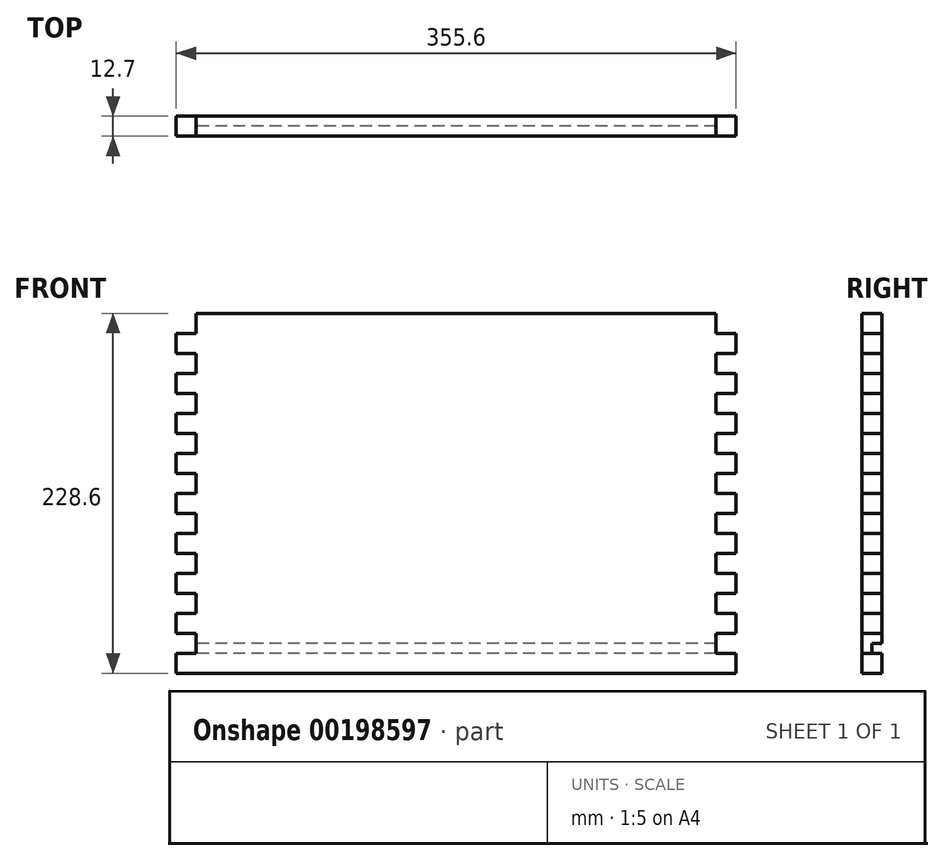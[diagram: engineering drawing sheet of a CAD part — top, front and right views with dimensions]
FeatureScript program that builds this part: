
annotation { "Feature Type Name" : "Feature", "Feature Type Description" : "" }
export const myFeature = defineFeature(function(context is Context, id is Id, definition is map)
    precondition{}
    {
        {
            var Q0;
            Q0=qCreatedBy(makeId("Front.planeOp"),FACE);
            var sketch = newSketch(context, id + "F0", { "sketchPlane" : qUnion([Q0])});
            skLineSegment(sketch, "E0.bottom", {"start": v(0, 0) * mm, "end": v(355.6, 0) * mm});
            skLineSegment(sketch, "E0.top", {"start": v(0, 228.6) * mm, "end": v(355.6, 228.6) * mm});
            skLineSegment(sketch, "E0.left", {"start": v(0, 0) * mm, "end": v(0, 228.6) * mm});
            skLineSegment(sketch, "E0.right", {"start": v(355.6, 0) * mm, "end": v(355.6, 228.6) * mm});
            skSolve(sketch);
        }
        {
            var Q0;
            Q0 = qSketchRegion(id + "F0", true);
            extrude(context, id + "F1", {"entities" : qUnion([Q0]), "depth" : 12.7 * mm});
        }
        {
            var Q0;
            Q0=makeQuery(id+"F1.opExtrude","CAP_FACE",FACE,{"disambiguationData":[OSD([sQuery(id+"F0.wireOp",EDGE,"E0.bottom"),sQuery(id+"F0.wireOp",EDGE,"E0.top"),sQuery(id+"F0.wireOp",EDGE,"E0.left"),sQuery(id+"F0.wireOp",EDGE,"E0.right")])],"isStart":false});
            var sketch = newSketch(context, id + "F2", { "sketchPlane" : qUnion([Q0])});
            skLineSegment(sketch, "E1", {"start": v(0, 228.6) * mm, "end": v(12.7, 228.6) * mm});
            skLineSegment(sketch, "E2.bottom", {"start": v(12.7, 228.6) * mm, "end": v(0, 228.6) * mm});
            skLineSegment(sketch, "E2.top", {"start": v(12.7, 215.9) * mm, "end": v(0, 215.9) * mm});
            skLineSegment(sketch, "E2.left", {"start": v(12.7, 228.6) * mm, "end": v(12.7, 215.9) * mm});
            skLineSegment(sketch, "E2.right", {"start": v(0, 228.6) * mm, "end": v(0, 215.9) * mm});
            skLineSegment(sketch, "E3.0.1.0", {"start": v(12.7, 190.5) * mm, "end": v(0, 190.5) * mm});
            skLineSegment(sketch, "E3.0.1.1", {"start": v(12.7, 203.2) * mm, "end": v(12.7, 190.5) * mm});
            skLineSegment(sketch, "E3.0.1.2", {"start": v(12.7, 203.2) * mm, "end": v(0, 203.2) * mm});
            skLineSegment(sketch, "E3.0.1.3", {"start": v(0, 203.2) * mm, "end": v(0, 190.5) * mm});
            skLineSegment(sketch, "E3.0.2.0", {"start": v(12.7, 165.1) * mm, "end": v(0, 165.1) * mm});
            skLineSegment(sketch, "E3.0.2.1", {"start": v(12.7, 177.8) * mm, "end": v(12.7, 165.1) * mm});
            skLineSegment(sketch, "E3.0.2.2", {"start": v(12.7, 177.8) * mm, "end": v(0, 177.8) * mm});
            skLineSegment(sketch, "E3.0.2.3", {"start": v(0, 177.8) * mm, "end": v(0, 165.1) * mm});
            skLineSegment(sketch, "E3.0.3.0", {"start": v(12.7, 139.7) * mm, "end": v(0, 139.7) * mm});
            skLineSegment(sketch, "E3.0.3.1", {"start": v(12.7, 152.4) * mm, "end": v(12.7, 139.7) * mm});
            skLineSegment(sketch, "E3.0.3.2", {"start": v(12.7, 152.4) * mm, "end": v(0, 152.4) * mm});
            skLineSegment(sketch, "E3.0.3.3", {"start": v(0, 152.4) * mm, "end": v(0, 139.7) * mm});
            skLineSegment(sketch, "E3.0.4.0", {"start": v(12.7, 114.3) * mm, "end": v(0, 114.3) * mm});
            skLineSegment(sketch, "E3.0.4.1", {"start": v(12.7, 127) * mm, "end": v(12.7, 114.3) * mm});
            skLineSegment(sketch, "E3.0.4.2", {"start": v(12.7, 127) * mm, "end": v(0, 127) * mm});
            skLineSegment(sketch, "E3.0.4.3", {"start": v(0, 127) * mm, "end": v(0, 114.3) * mm});
            skLineSegment(sketch, "E3.0.5.0", {"start": v(12.7, 88.9) * mm, "end": v(0, 88.9) * mm});
            skLineSegment(sketch, "E3.0.5.1", {"start": v(12.7, 101.6) * mm, "end": v(12.7, 88.9) * mm});
            skLineSegment(sketch, "E3.0.5.2", {"start": v(12.7, 101.6) * mm, "end": v(0, 101.6) * mm});
            skLineSegment(sketch, "E3.0.5.3", {"start": v(0, 101.6) * mm, "end": v(0, 88.9) * mm});
            skLineSegment(sketch, "E3.0.6.0", {"start": v(12.7, 63.5) * mm, "end": v(0, 63.5) * mm});
            skLineSegment(sketch, "E3.0.6.1", {"start": v(12.7, 76.2) * mm, "end": v(12.7, 63.5) * mm});
            skLineSegment(sketch, "E3.0.6.2", {"start": v(12.7, 76.2) * mm, "end": v(0, 76.2) * mm});
            skLineSegment(sketch, "E3.0.6.3", {"start": v(0, 76.2) * mm, "end": v(0, 63.5) * mm});
            skLineSegment(sketch, "E3.0.7.0", {"start": v(12.7, 38.1) * mm, "end": v(0, 38.1) * mm});
            skLineSegment(sketch, "E3.0.7.1", {"start": v(12.7, 50.8) * mm, "end": v(12.7, 38.1) * mm});
            skLineSegment(sketch, "E3.0.7.2", {"start": v(12.7, 50.8) * mm, "end": v(0, 50.8) * mm});
            skLineSegment(sketch, "E3.0.7.3", {"start": v(0, 50.8) * mm, "end": v(0, 38.1) * mm});
            skLineSegment(sketch, "E3.0.8.0", {"start": v(12.7, 12.7) * mm, "end": v(0, 12.7) * mm});
            skLineSegment(sketch, "E3.0.8.1", {"start": v(12.7, 25.4) * mm, "end": v(12.7, 12.7) * mm});
            skLineSegment(sketch, "E3.0.8.2", {"start": v(12.7, 25.4) * mm, "end": v(0, 25.4) * mm});
            skLineSegment(sketch, "E3.0.8.3", {"start": v(0, 25.4) * mm, "end": v(0, 12.7) * mm});
            skLineSegment(sketch, "E3.1.1.0", {"start": v(12.7, 190.5) * mm, "end": v(0, 190.5) * mm});
            skLineSegment(sketch, "E3.1.1.1", {"start": v(12.7, 203.2) * mm, "end": v(12.7, 190.5) * mm});
            skLineSegment(sketch, "E3.1.1.2", {"start": v(12.7, 203.2) * mm, "end": v(0, 203.2) * mm});
            skLineSegment(sketch, "E3.1.1.3", {"start": v(0, 203.2) * mm, "end": v(0, 190.5) * mm});
            skLineSegment(sketch, "E3.1.2.0", {"start": v(12.7, 165.1) * mm, "end": v(0, 165.1) * mm});
            skLineSegment(sketch, "E3.1.2.1", {"start": v(12.7, 177.8) * mm, "end": v(12.7, 165.1) * mm});
            skLineSegment(sketch, "E3.1.2.2", {"start": v(12.7, 177.8) * mm, "end": v(0, 177.8) * mm});
            skLineSegment(sketch, "E3.1.2.3", {"start": v(0, 177.8) * mm, "end": v(0, 165.1) * mm});
            skLineSegment(sketch, "E3.1.3.0", {"start": v(12.7, 139.7) * mm, "end": v(0, 139.7) * mm});
            skLineSegment(sketch, "E3.1.3.1", {"start": v(12.7, 152.4) * mm, "end": v(12.7, 139.7) * mm});
            skLineSegment(sketch, "E3.1.3.2", {"start": v(12.7, 152.4) * mm, "end": v(0, 152.4) * mm});
            skLineSegment(sketch, "E3.1.3.3", {"start": v(0, 152.4) * mm, "end": v(0, 139.7) * mm});
            skLineSegment(sketch, "E3.1.4.0", {"start": v(12.7, 114.3) * mm, "end": v(0, 114.3) * mm});
            skLineSegment(sketch, "E3.1.4.1", {"start": v(12.7, 127) * mm, "end": v(12.7, 114.3) * mm});
            skLineSegment(sketch, "E3.1.4.2", {"start": v(12.7, 127) * mm, "end": v(0, 127) * mm});
            skLineSegment(sketch, "E3.1.4.3", {"start": v(0, 127) * mm, "end": v(0, 114.3) * mm});
            skLineSegment(sketch, "E3.1.5.0", {"start": v(12.7, 88.9) * mm, "end": v(0, 88.9) * mm});
            skLineSegment(sketch, "E3.1.5.1", {"start": v(12.7, 101.6) * mm, "end": v(12.7, 88.9) * mm});
            skLineSegment(sketch, "E3.1.5.2", {"start": v(12.7, 101.6) * mm, "end": v(0, 101.6) * mm});
            skLineSegment(sketch, "E3.1.5.3", {"start": v(0, 101.6) * mm, "end": v(0, 88.9) * mm});
            skLineSegment(sketch, "E3.1.6.0", {"start": v(12.7, 63.5) * mm, "end": v(0, 63.5) * mm});
            skLineSegment(sketch, "E3.1.6.1", {"start": v(12.7, 76.2) * mm, "end": v(12.7, 63.5) * mm});
            skLineSegment(sketch, "E3.1.6.2", {"start": v(12.7, 76.2) * mm, "end": v(0, 76.2) * mm});
            skLineSegment(sketch, "E3.1.6.3", {"start": v(0, 76.2) * mm, "end": v(0, 63.5) * mm});
            skLineSegment(sketch, "E3.1.7.0", {"start": v(12.7, 38.1) * mm, "end": v(0, 38.1) * mm});
            skLineSegment(sketch, "E3.1.7.1", {"start": v(12.7, 50.8) * mm, "end": v(12.7, 38.1) * mm});
            skLineSegment(sketch, "E3.1.7.2", {"start": v(12.7, 50.8) * mm, "end": v(0, 50.8) * mm});
            skLineSegment(sketch, "E3.1.7.3", {"start": v(0, 50.8) * mm, "end": v(0, 38.1) * mm});
            skLineSegment(sketch, "E3.1.8.0", {"start": v(12.7, 12.7) * mm, "end": v(0, 12.7) * mm});
            skLineSegment(sketch, "E3.1.8.1", {"start": v(12.7, 25.4) * mm, "end": v(12.7, 12.7) * mm});
            skLineSegment(sketch, "E3.1.8.2", {"start": v(12.7, 25.4) * mm, "end": v(0, 25.4) * mm});
            skLineSegment(sketch, "E3.1.8.3", {"start": v(0, 25.4) * mm, "end": v(0, 12.7) * mm});
            skLineSegment(sketch, "E3.2.1.0", {"start": v(12.7, 190.5) * mm, "end": v(0, 190.5) * mm});
            skLineSegment(sketch, "E3.2.1.1", {"start": v(12.7, 203.2) * mm, "end": v(12.7, 190.5) * mm});
            skLineSegment(sketch, "E3.2.1.2", {"start": v(12.7, 203.2) * mm, "end": v(0, 203.2) * mm});
            skLineSegment(sketch, "E3.2.1.3", {"start": v(0, 203.2) * mm, "end": v(0, 190.5) * mm});
            skLineSegment(sketch, "E3.2.2.0", {"start": v(12.7, 165.1) * mm, "end": v(0, 165.1) * mm});
            skLineSegment(sketch, "E3.2.2.1", {"start": v(12.7, 177.8) * mm, "end": v(12.7, 165.1) * mm});
            skLineSegment(sketch, "E3.2.2.2", {"start": v(12.7, 177.8) * mm, "end": v(0, 177.8) * mm});
            skLineSegment(sketch, "E3.2.2.3", {"start": v(0, 177.8) * mm, "end": v(0, 165.1) * mm});
            skLineSegment(sketch, "E3.2.3.0", {"start": v(12.7, 139.7) * mm, "end": v(0, 139.7) * mm});
            skLineSegment(sketch, "E3.2.3.1", {"start": v(12.7, 152.4) * mm, "end": v(12.7, 139.7) * mm});
            skLineSegment(sketch, "E3.2.3.2", {"start": v(12.7, 152.4) * mm, "end": v(0, 152.4) * mm});
            skLineSegment(sketch, "E3.2.3.3", {"start": v(0, 152.4) * mm, "end": v(0, 139.7) * mm});
            skLineSegment(sketch, "E3.2.4.0", {"start": v(12.7, 114.3) * mm, "end": v(0, 114.3) * mm});
            skLineSegment(sketch, "E3.2.4.1", {"start": v(12.7, 127) * mm, "end": v(12.7, 114.3) * mm});
            skLineSegment(sketch, "E3.2.4.2", {"start": v(12.7, 127) * mm, "end": v(0, 127) * mm});
            skLineSegment(sketch, "E3.2.4.3", {"start": v(0, 127) * mm, "end": v(0, 114.3) * mm});
            skLineSegment(sketch, "E3.2.5.0", {"start": v(12.7, 88.9) * mm, "end": v(0, 88.9) * mm});
            skLineSegment(sketch, "E3.2.5.1", {"start": v(12.7, 101.6) * mm, "end": v(12.7, 88.9) * mm});
            skLineSegment(sketch, "E3.2.5.2", {"start": v(12.7, 101.6) * mm, "end": v(0, 101.6) * mm});
            skLineSegment(sketch, "E3.2.5.3", {"start": v(0, 101.6) * mm, "end": v(0, 88.9) * mm});
            skLineSegment(sketch, "E3.2.6.0", {"start": v(12.7, 63.5) * mm, "end": v(0, 63.5) * mm});
            skLineSegment(sketch, "E3.2.6.1", {"start": v(12.7, 76.2) * mm, "end": v(12.7, 63.5) * mm});
            skLineSegment(sketch, "E3.2.6.2", {"start": v(12.7, 76.2) * mm, "end": v(0, 76.2) * mm});
            skLineSegment(sketch, "E3.2.6.3", {"start": v(0, 76.2) * mm, "end": v(0, 63.5) * mm});
            skLineSegment(sketch, "E3.2.7.0", {"start": v(12.7, 38.1) * mm, "end": v(0, 38.1) * mm});
            skLineSegment(sketch, "E3.2.7.1", {"start": v(12.7, 50.8) * mm, "end": v(12.7, 38.1) * mm});
            skLineSegment(sketch, "E3.2.7.2", {"start": v(12.7, 50.8) * mm, "end": v(0, 50.8) * mm});
            skLineSegment(sketch, "E3.2.7.3", {"start": v(0, 50.8) * mm, "end": v(0, 38.1) * mm});
            skLineSegment(sketch, "E3.2.8.0", {"start": v(12.7, 12.7) * mm, "end": v(0, 12.7) * mm});
            skLineSegment(sketch, "E3.2.8.1", {"start": v(12.7, 25.4) * mm, "end": v(12.7, 12.7) * mm});
            skLineSegment(sketch, "E3.2.8.2", {"start": v(12.7, 25.4) * mm, "end": v(0, 25.4) * mm});
            skLineSegment(sketch, "E3.2.8.3", {"start": v(0, 25.4) * mm, "end": v(0, 12.7) * mm});
            skLineSegment(sketch, "E3.direction1", {"start": v(0, 215.9) * mm, "end": v(0, 215.9) * mm});
            skLineSegment(sketch, "E3.direction2", {"start": v(0, 215.9) * mm, "end": v(0, 190.5) * mm, "construction": true});
            skPoint(sketch, "E4.endSnap0", {"position": v(177.8, 228.6) * mm});
            skLineSegment(sketch, "E5.MirrorCS", {"start": v(342.9, 228.6) * mm, "end": v(352.43, 228.6) * mm});
            skLineSegment(sketch, "E6.MirrorCS", {"start": v(346.07, 215.9) * mm, "end": v(355.6, 215.9) * mm});
            skLineSegment(sketch, "E7.MirrorCS", {"start": v(346.07, 228.6) * mm, "end": v(355.6, 228.6) * mm});
            skLineSegment(sketch, "E8.MirrorCS", {"start": v(355.6, 228.6) * mm, "end": v(355.6, 215.9) * mm});
            skLineSegment(sketch, "E9.MirrorCS", {"start": v(355.6, 228.6) * mm, "end": v(346.07, 228.6) * mm});
            skLineSegment(sketch, "E10.MirrorCS", {"start": v(342.9, 215.9) * mm, "end": v(352.43, 215.9) * mm});
            skLineSegment(sketch, "E11.MirrorCS", {"start": v(342.9, 228.6) * mm, "end": v(342.9, 215.9) * mm});
            skLineSegment(sketch, "E12.MirrorCS", {"start": v(355.6, 215.9) * mm, "end": v(355.6, 215.9) * mm});
            skLineSegment(sketch, "E13", {"start": v(355.6, 228.6) * mm, "end": v(342.9, 228.6) * mm});
            skPoint(sketch, "E14.startSnap0", {"position": v(342.9, 222.25) * mm});
            skLineSegment(sketch, "E15.bottom", {"start": v(355.6, 203.14) * mm, "end": v(342.9, 203.14) * mm});
            skLineSegment(sketch, "E15.top", {"start": v(355.6, 190.44) * mm, "end": v(342.9, 190.44) * mm});
            skLineSegment(sketch, "E15.right", {"start": v(342.9, 203.14) * mm, "end": v(342.9, 190.44) * mm});
            skLineSegment(sketch, "E16", {"start": v(355.6, 203.14) * mm, "end": v(355.6, 190.44) * mm});
            skLineSegment(sketch, "E17.0.1.0", {"start": v(355.6, 165.04) * mm, "end": v(342.9, 165.04) * mm});
            skLineSegment(sketch, "E17.0.1.1", {"start": v(355.6, 177.74) * mm, "end": v(355.6, 165.04) * mm});
            skLineSegment(sketch, "E17.0.1.2", {"start": v(342.9, 177.74) * mm, "end": v(342.9, 165.04) * mm});
            skLineSegment(sketch, "E17.0.1.3", {"start": v(355.6, 177.74) * mm, "end": v(342.9, 177.74) * mm});
            skLineSegment(sketch, "E17.0.2.0", {"start": v(355.6, 139.64) * mm, "end": v(342.9, 139.64) * mm});
            skLineSegment(sketch, "E17.0.2.1", {"start": v(355.6, 152.34) * mm, "end": v(355.6, 139.64) * mm});
            skLineSegment(sketch, "E17.0.2.2", {"start": v(342.9, 152.34) * mm, "end": v(342.9, 139.64) * mm});
            skLineSegment(sketch, "E17.0.2.3", {"start": v(355.6, 152.34) * mm, "end": v(342.9, 152.34) * mm});
            skLineSegment(sketch, "E17.0.3.0", {"start": v(355.6, 114.24) * mm, "end": v(342.9, 114.24) * mm});
            skLineSegment(sketch, "E17.0.3.1", {"start": v(355.6, 126.94) * mm, "end": v(355.6, 114.24) * mm});
            skLineSegment(sketch, "E17.0.3.2", {"start": v(342.9, 126.94) * mm, "end": v(342.9, 114.24) * mm});
            skLineSegment(sketch, "E17.0.3.3", {"start": v(355.6, 126.94) * mm, "end": v(342.9, 126.94) * mm});
            skLineSegment(sketch, "E17.0.4.0", {"start": v(355.6, 88.84) * mm, "end": v(342.9, 88.84) * mm});
            skLineSegment(sketch, "E17.0.4.1", {"start": v(355.6, 101.54) * mm, "end": v(355.6, 88.84) * mm});
            skLineSegment(sketch, "E17.0.4.2", {"start": v(342.9, 101.54) * mm, "end": v(342.9, 88.84) * mm});
            skLineSegment(sketch, "E17.0.4.3", {"start": v(355.6, 101.54) * mm, "end": v(342.9, 101.54) * mm});
            skLineSegment(sketch, "E17.0.5.0", {"start": v(355.6, 63.44) * mm, "end": v(342.9, 63.44) * mm});
            skLineSegment(sketch, "E17.0.5.1", {"start": v(355.6, 76.14) * mm, "end": v(355.6, 63.44) * mm});
            skLineSegment(sketch, "E17.0.5.2", {"start": v(342.9, 76.14) * mm, "end": v(342.9, 63.44) * mm});
            skLineSegment(sketch, "E17.0.5.3", {"start": v(355.6, 76.14) * mm, "end": v(342.9, 76.14) * mm});
            skLineSegment(sketch, "E17.0.6.0", {"start": v(355.6, 38.04) * mm, "end": v(342.9, 38.04) * mm});
            skLineSegment(sketch, "E17.0.6.1", {"start": v(355.6, 50.74) * mm, "end": v(355.6, 38.04) * mm});
            skLineSegment(sketch, "E17.0.6.2", {"start": v(342.9, 50.74) * mm, "end": v(342.9, 38.04) * mm});
            skLineSegment(sketch, "E17.0.6.3", {"start": v(355.6, 50.74) * mm, "end": v(342.9, 50.74) * mm});
            skLineSegment(sketch, "E17.0.7.0", {"start": v(355.6, 12.64) * mm, "end": v(342.9, 12.64) * mm});
            skLineSegment(sketch, "E17.0.7.1", {"start": v(355.6, 25.34) * mm, "end": v(355.6, 12.64) * mm});
            skLineSegment(sketch, "E17.0.7.2", {"start": v(342.9, 25.34) * mm, "end": v(342.9, 12.64) * mm});
            skLineSegment(sketch, "E17.0.7.3", {"start": v(355.6, 25.34) * mm, "end": v(342.9, 25.34) * mm});
            skSolve(sketch);
        }
        {
            var Q0;
            Q0 = qSketchRegion(id + "F2", true);
            extrude(context, id + "F3", {"entities" : qUnion([Q0]), "operationType" : NewBodyOperationType.REMOVE, "oppositeDirection" : true, "depth" : 25.4 * mm});
        }
        {
            var Q0;
            Q0=makeQuery(id+"F1.opExtrude","CAP_FACE",FACE,{"disambiguationData":[OSD([sQuery(id+"F0.wireOp",EDGE,"E0.bottom"),sQuery(id+"F0.wireOp",EDGE,"E0.top"),sQuery(id+"F0.wireOp",EDGE,"E0.left"),sQuery(id+"F0.wireOp",EDGE,"E0.right")])],"isStart":true});
            var sketch = newSketch(context, id + "F4", { "sketchPlane" : qUnion([Q0])});
            skLineSegment(sketch, "E18.bottom", {"start": v(-342.9, 12.7) * mm, "end": v(-12.7, 12.7) * mm});
            skLineSegment(sketch, "E18.top", {"start": v(-342.9, 19.05) * mm, "end": v(-12.7, 19.05) * mm});
            skLineSegment(sketch, "E18.left", {"start": v(-342.9, 12.7) * mm, "end": v(-342.9, 19.05) * mm});
            skLineSegment(sketch, "E18.right", {"start": v(-12.7, 12.7) * mm, "end": v(-12.7, 19.05) * mm});
            skSolve(sketch);
        }
        {
            var Q0;
            Q0 = qSketchRegion(id + "F4", true);
            extrude(context, id + "F5", {"entities" : qUnion([Q0]), "operationType" : NewBodyOperationType.REMOVE, "oppositeDirection" : true, "depth" : 6.35 * mm});
        }
    });
